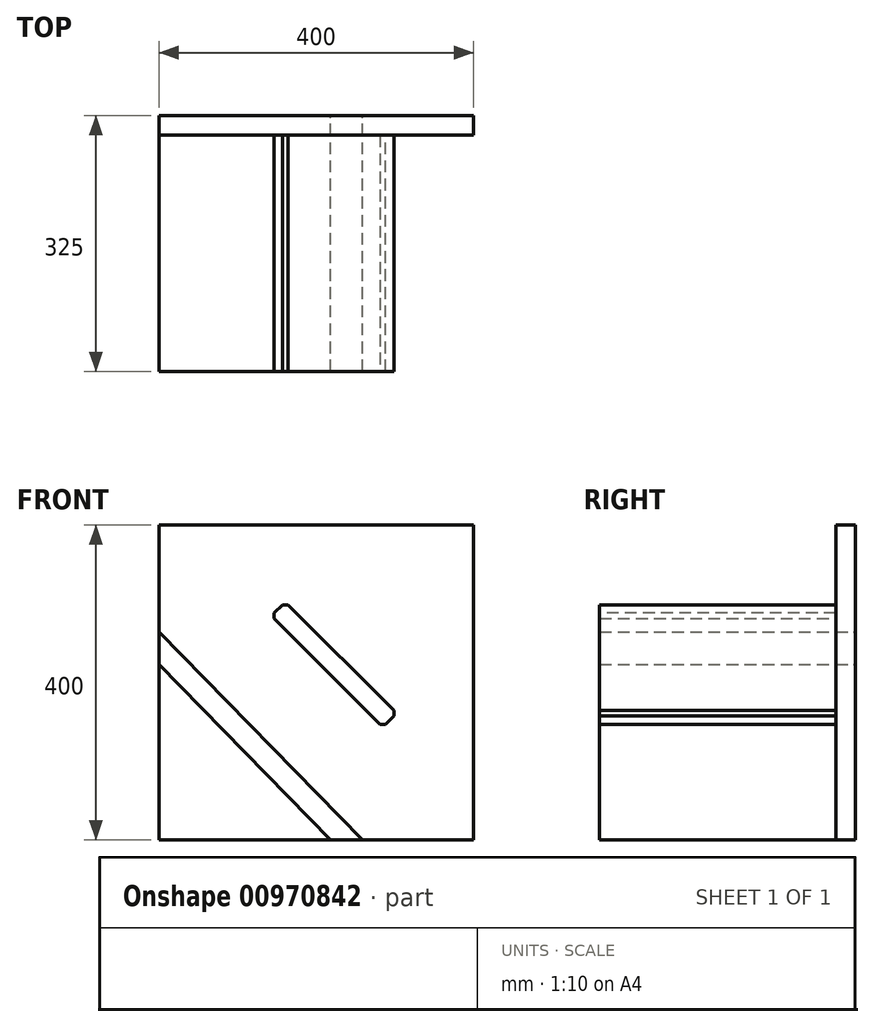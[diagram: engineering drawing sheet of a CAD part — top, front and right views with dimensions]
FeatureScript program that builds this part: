
annotation { "Feature Type Name" : "Feature", "Feature Type Description" : "" }
export const myFeature = defineFeature(function(context is Context, id is Id, definition is map)
    precondition{}
    {
        {
            var Q0;
            Q0=qCreatedBy(makeId("Front.planeOp"),FACE);
            var sketch = newSketch(context, id + "F0", { "sketchPlane" : qUnion([Q0])});
            skLineSegment(sketch, "E0.bottom", {"start": v(-263.5, 325.88) * mm, "end": v(136.5, 325.88) * mm});
            skLineSegment(sketch, "E0.top", {"start": v(-263.5, -74.12) * mm, "end": v(136.5, -74.12) * mm});
            skLineSegment(sketch, "E0.left", {"start": v(-263.5, 325.88) * mm, "end": v(-263.5, -74.12) * mm});
            skLineSegment(sketch, "E0.right", {"start": v(136.5, 325.88) * mm, "end": v(136.5, -74.12) * mm});
            skLineSegment(sketch, "E1", {"start": v(38.65, 86.7) * mm, "end": v(-102.77, 228.12) * mm});
            skLineSegment(sketch, "E2", {"start": v(38.65, 86.7) * mm, "end": v(20.97, 69.02) * mm});
            skLineSegment(sketch, "E3", {"start": v(-102.77, 228.12) * mm, "end": v(-120.45, 210.45) * mm});
            skLineSegment(sketch, "E4", {"start": v(-120.45, 210.45) * mm, "end": v(20.97, 69.02) * mm});
            skLineSegment(sketch, "E5", {"start": v(136.5, -74.12) * mm, "end": v(136.5, -51.76) * mm});
            skLineSegment(sketch, "E6", {"start": v(-263.5, 190.3) * mm, "end": v(-4.74, -74.16) * mm});
            skLineSegment(sketch, "E7", {"start": v(-152.13, 34.7) * mm, "end": v(-45.65, -74.12) * mm});
            skLineSegment(sketch, "E8", {"start": v(-152.13, 34.7) * mm, "end": v(-263.5, 148.53) * mm});
            skSolve(sketch);
        }
        {
            var Q0;
            {var subQ1=sQuery(id+"F0.wireOp",EDGE,"E0.bottom");Q0=makeQuery(id+"F0.imprint","IMPRINT",FACE,{"disambiguationData":[TD([[makeQuery(id+"F0.imprint","IMPRINT",EDGE,{"derivedFrom":subQ1}),-1.0]])]});}
            var Q1;
            {var subQ0=sQuery(id+"F0.wireOp",EDGE,"E0.left");var subQ1=sQuery(id+"F0.wireOp",EDGE,"E0.top");var subQ2=makeQuery(id+"F0.imprint","INTERSECT",VERTEX,{"derivedFrom":[subQ1,subQ0]});Q1=makeQuery(id+"F0.imprint","IMPRINT",FACE,{"disambiguationData":[TD([[makeQuery(id+"F0.imprint","IMPRINT",EDGE,{"disambiguationData":[TD([[subQ2,-1.0]])],"derivedFrom":subQ1}),1.0]])]});}
            extrude(context, id + "F1", {"entities" : qUnion([Q0, Q1]), "depth" : 25 * mm, "offsetDistance" : 25 * mm});
        }
        {
            var Q0;
            {var subQ3=sQuery(id+"F0.wireOp",EDGE,"E0.top");var subQ5=sQuery(id+"F0.wireOp",EDGE,"E7");var subQ6=makeQuery(id+"F0.imprint","INTERSECT",VERTEX,{"derivedFrom":[subQ3,subQ5]});Q0=makeQuery(id+"F0.imprint","IMPRINT",FACE,{"disambiguationData":[TD([[makeQuery(id+"F0.imprint","IMPRINT",EDGE,{"disambiguationData":[TD([[subQ6,-1.0]])],"derivedFrom":subQ3}),1.0]])]});}
            extrude(context, id + "F2", {"entities" : qUnion([Q0]), "depth" : 325 * mm, "offsetDistance" : 25 * mm});
        }
        {
            var Q0;
            Q0=makeQuery(id+"F0.imprint","IMPRINT",FACE,{"disambiguationData":[TD([[makeQuery(id+"F0.imprint","IMPRINT",EDGE,{"derivedFrom":sQuery(id+"F0.wireOp",EDGE,"E1")}),1.0]])]});
            extrude(context, id + "F3", {"entities" : qUnion([Q0]), "operationType" : NewBodyOperationType.ADD, "depth" : 325 * mm, "offsetDistance" : 25 * mm});
        }
        {
            var Q0;
            Q0=makeQuery(id+"F3.opExtrude","SWEPT_EDGE",EDGE,{"disambiguationData":[OSD([sQuery(id+"F0.wireOp",EDGE,"E1"),sQuery(id+"F0.wireOp",EDGE,"E2")])]});
            var Q1;
            Q1=makeQuery(id+"F3.opExtrude","SWEPT_EDGE",EDGE,{"disambiguationData":[OSD([sQuery(id+"F0.wireOp",EDGE,"E2"),sQuery(id+"F0.wireOp",EDGE,"E4")])]});
            var Q2;
            Q2=makeQuery(id+"F3.opExtrude","SWEPT_EDGE",EDGE,{"disambiguationData":[OSD([sQuery(id+"F0.wireOp",EDGE,"E1"),sQuery(id+"F0.wireOp",EDGE,"E3")])]});
            var Q3;
            Q3=makeQuery(id+"F3.opExtrude","SWEPT_EDGE",EDGE,{"disambiguationData":[OSD([sQuery(id+"F0.wireOp",EDGE,"E3"),sQuery(id+"F0.wireOp",EDGE,"E4")])]});
            chamfer(context, id + "F4", {"entities" : qUnion([Q0, Q1, Q2, Q3]), "width" : 5 * mm, "tangentPropagation" : true});
        }
    });
